# Revit family: 3-653-xxx Magnum Pendant
name_source: partatom
category: Lighting Fixtures
units: mm (PartAtom-declared; Revit-internal decimal feet)

## family parameters
Always vertical = Yes
Cut with Voids When Loaded = No
Host = Ceiling
Light Source = Yes
OmniClass Number = 23.80.70.11
OmniClass Title = Luminaries for Internal Lighting
Part Type = Normal
Room Calculation Point = No
Round Connector Dimension = Use Diameter
Shared = No

## types (8) — shared parameters
Color Filter = 16777215
Dimming Lamp Color Temperature Shift = <None>
Lamp = LED
Main Diffuser = Matte Opal Glass
Manufacturer = Oxygen Lighting
Model = 3-653-xxx Magnum (Pendant)
Photometric Web File = 3-653-114 Magnum Pendant.ies
References = Ref. 3 = 120 V / Ref. 37 = 277 V
Tilt Angle = 90.00°
Voltage Input = 120 V or 277 V - 50/60 Hz
Wattage Comments = 6.62 W at 120 V
zero-valued in all types: Default Elevation

## per-type parameters (varying)
| type | Metal Finish | Voltage |
| 3-653-114 - Polished Chrome / Matte Opal Glass | 14 - Polished Chrome | 120 V |
| 3-653-124 - Satin Nickel / Matte Opal Glass | 24 - Satin Nickel | 120 V |
| 3-653-140 - Aged Brass / Matte Opal Glass | 40 - Aged Brass | 120 V |
| 37-653-114 - Polished Chrome / Matte Opal Glass | 14 - Polished Chrome | 277 V |
| 37-653-124 - Satin Nickel / Matte Opal Glass | 24 - Satin Nickel | 277 V |
| 37-653-140 - Aged Brass / Matte Opal Glass | 40 - Aged Brass | 277 V |
| 3-653-125 - Satin Copper / Matte Opal Glass | 25 - Satin Copper | 120 V |
| 37-653-125 - Satin Copper / Matte Opal Glass | 25 - Satin Copper | 277 V |

## geometry (parser evidence)
native form markers: Sweep x2
no freeform markers — native parametric forms only
